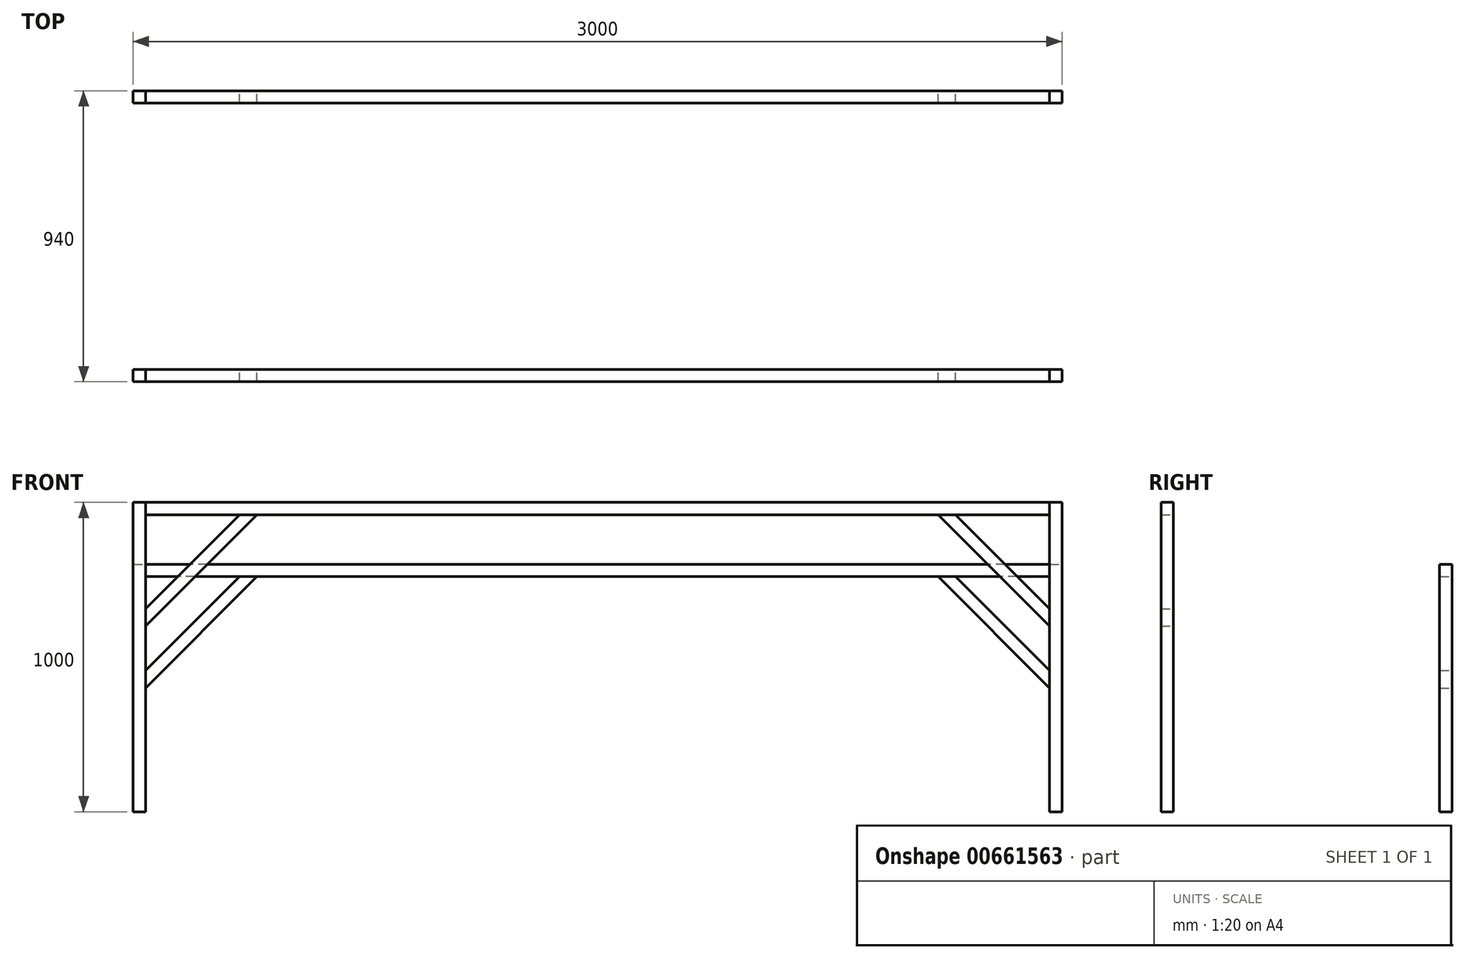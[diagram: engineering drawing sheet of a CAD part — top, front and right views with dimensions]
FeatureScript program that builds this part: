
annotation { "Feature Type Name" : "Feature", "Feature Type Description" : "" }
export const myFeature = defineFeature(function(context is Context, id is Id, definition is map)
    precondition{}
    {
        {
            var Q0;
            Q0=qCreatedBy(makeId("Top.planeOp"),FACE);
            var sketch = newSketch(context, id + "F0", { "sketchPlane" : qUnion([Q0])});
            skLineSegment(sketch, "E0.bottom", {"start": v(0, 0) * mm, "end": v(40, 0) * mm});
            skLineSegment(sketch, "E0.top", {"start": v(0, -40) * mm, "end": v(40, -40) * mm});
            skLineSegment(sketch, "E0.left", {"start": v(0, 0) * mm, "end": v(0, -40) * mm});
            skLineSegment(sketch, "E0.right", {"start": v(40, 0) * mm, "end": v(40, -40) * mm});
            skLineSegment(sketch, "E1.0.1.0", {"start": v(40, -900) * mm, "end": v(40, -940) * mm});
            skLineSegment(sketch, "E1.0.1.1", {"start": v(0, -900) * mm, "end": v(0, -940) * mm});
            skLineSegment(sketch, "E1.0.1.2", {"start": v(0, -900) * mm, "end": v(40, -900) * mm});
            skLineSegment(sketch, "E1.0.1.3", {"start": v(0, -940) * mm, "end": v(40, -940) * mm});
            skLineSegment(sketch, "E1.1.0.0", {"start": v(3000, 0) * mm, "end": v(3000, -40) * mm});
            skLineSegment(sketch, "E1.1.0.1", {"start": v(2960, 0) * mm, "end": v(2960, -40) * mm});
            skLineSegment(sketch, "E1.1.0.2", {"start": v(2960, 0) * mm, "end": v(3000, 0) * mm});
            skLineSegment(sketch, "E1.1.0.3", {"start": v(2960, -40) * mm, "end": v(3000, -40) * mm});
            skLineSegment(sketch, "E1.1.1.0", {"start": v(3000, -900) * mm, "end": v(3000, -940) * mm});
            skLineSegment(sketch, "E1.1.1.1", {"start": v(2960, -900) * mm, "end": v(2960, -940) * mm});
            skLineSegment(sketch, "E1.1.1.2", {"start": v(2960, -900) * mm, "end": v(3000, -900) * mm});
            skLineSegment(sketch, "E1.1.1.3", {"start": v(2960, -940) * mm, "end": v(3000, -940) * mm});
            skLineSegment(sketch, "E1.direction1", {"start": v(0, -40) * mm, "end": v(2960, -40) * mm, "construction": true});
            skLineSegment(sketch, "E1.direction2", {"start": v(0, -40) * mm, "end": v(0, -940) * mm, "construction": true});
            skSolve(sketch);
        }
        {
            var Q0;
            Q0=makeQuery(id+"F0.imprint","IMPRINT",FACE,{"disambiguationData":[TD([[makeQuery(id+"F0.imprint","IMPRINT",EDGE,{"derivedFrom":sQuery(id+"F0.wireOp",EDGE,"E0.bottom")}),-1.0]])]});
            var Q1;
            Q1=makeQuery(id+"F0.imprint","IMPRINT",FACE,{"disambiguationData":[TD([[makeQuery(id+"F0.imprint","IMPRINT",EDGE,{"derivedFrom":sQuery(id+"F0.wireOp",EDGE,"E1.1.0.0")}),-1.0]])]});
            extrude(context, id + "F1", {"entities" : qUnion([Q0, Q1]), "depth" : 800 * mm, "offsetDistance" : 25 * mm});
        }
        {
            var Q0;
            Q0=makeQuery(id+"F0.imprint","IMPRINT",FACE,{"disambiguationData":[TD([[makeQuery(id+"F0.imprint","IMPRINT",EDGE,{"derivedFrom":sQuery(id+"F0.wireOp",EDGE,"E1.0.1.0")}),-1.0]])]});
            var Q1;
            Q1=makeQuery(id+"F0.imprint","IMPRINT",FACE,{"disambiguationData":[TD([[makeQuery(id+"F0.imprint","IMPRINT",EDGE,{"derivedFrom":sQuery(id+"F0.wireOp",EDGE,"E1.1.1.0")}),-1.0]])]});
            extrude(context, id + "F2", {"entities" : qUnion([Q0, Q1]), "depth" : 1000 * mm, "offsetDistance" : 25 * mm});
        }
        {
            var Q0;
            Q0=makeQuery(id+"F1.opExtrude","SWEPT_FACE",FACE,{"disambiguationData":[OSD([sQuery(id+"F0.wireOp",EDGE,"E0.right")])]});
            var sketch = newSketch(context, id + "F3", { "sketchPlane" : qUnion([Q0])});
            skLineSegment(sketch, "E2.bottom", {"start": v(-40, 800) * mm, "end": v(0, 800) * mm});
            skLineSegment(sketch, "E2.top", {"start": v(-40, 760) * mm, "end": v(0, 760) * mm});
            skLineSegment(sketch, "E2.left", {"start": v(-40, 800) * mm, "end": v(-40, 760) * mm});
            skLineSegment(sketch, "E2.right", {"start": v(0, 800) * mm, "end": v(0, 760) * mm});
            skSolve(sketch);
        }
        {
            var Q0;
            Q0=makeQuery(id+"F3.imprint","IMPRINT",FACE,{"disambiguationData":[TD([[makeQuery(id+"F3.imprint","IMPRINT",EDGE,{"derivedFrom":sQuery(id+"F3.wireOp",EDGE,"E2.bottom")}),1.0]])]});
            extrude(context, id + "F4", {"entities" : qUnion([Q0]), "endBound" : BoundingType.UP_TO_NEXT, "depth" : 25 * mm, "offsetDistance" : 25 * mm});
        }
        {
            var Q0;
            Q0=makeQuery(id+"F2.opExtrude","SWEPT_FACE",FACE,{"disambiguationData":[OSD([sQuery(id+"F0.wireOp",EDGE,"E1.0.1.0")])]});
            var sketch = newSketch(context, id + "F5", { "sketchPlane" : qUnion([Q0])});
            skLineSegment(sketch, "E3.bottom", {"start": v(-940, 1000) * mm, "end": v(-900, 1000) * mm});
            skLineSegment(sketch, "E3.top", {"start": v(-940, 960) * mm, "end": v(-900, 960) * mm});
            skLineSegment(sketch, "E3.left", {"start": v(-940, 1000) * mm, "end": v(-940, 960) * mm});
            skLineSegment(sketch, "E3.right", {"start": v(-900, 1000) * mm, "end": v(-900, 960) * mm});
            skSolve(sketch);
        }
        {
            var Q0;
            Q0=makeQuery(id+"F5.imprint","IMPRINT",FACE,{"disambiguationData":[TD([[makeQuery(id+"F5.imprint","IMPRINT",EDGE,{"derivedFrom":sQuery(id+"F5.wireOp",EDGE,"E3.bottom")}),1.0]])]});
            extrude(context, id + "F6", {"entities" : qUnion([Q0]), "endBound" : BoundingType.UP_TO_NEXT, "depth" : 25 * mm, "offsetDistance" : 25 * mm});
        }
        {
            var Q0;
            Q0=makeQuery(id+"F1.opExtrude","SWEPT_FACE",FACE,{"disambiguationData":[OSD([sQuery(id+"F0.wireOp",EDGE,"E0.bottom")])]});
            var sketch = newSketch(context, id + "F7", { "sketchPlane" : qUnion([Q0])});
            skLineSegment(sketch, "E4", {"start": v(-40, 456.57) * mm, "end": v(-343.43, 760) * mm});
            skLineSegment(sketch, "E5", {"start": v(-343.43, 760) * mm, "end": v(-400, 760) * mm});
            skLineSegment(sketch, "E6", {"start": v(-400, 760) * mm, "end": v(-40, 400) * mm});
            skLineSegment(sketch, "E7", {"start": v(-40, 400) * mm, "end": v(-40, 456.57) * mm});
            skSolve(sketch);
        }
        {
            var Q0;
            Q0=makeQuery(id+"F7.imprint","IMPRINT",FACE,{"disambiguationData":[TD([[makeQuery(id+"F7.imprint","IMPRINT",EDGE,{"derivedFrom":sQuery(id+"F7.wireOp",EDGE,"E4")}),1.0]])]});
            extrude(context, id + "F8", {"entities" : qUnion([Q0]), "oppositeDirection" : true, "depth" : 40 * mm, "offsetDistance" : 25 * mm});
        }
        {
            var Q0;
            Q0=qCreatedBy(makeId("Right.planeOp"),FACE);
            cPlane(context, id + "F9", {"entities" : qUnion([Q0]), "cplaneType" : CPlaneType.OFFSET, "offset" : 3000 / 2 * mm, "width" : 150 * mm, "height" : 150 * mm});
        }
        {
            var Q0;
            Q0=makeQuery(id+"F8.opExtrude","SWEPT_BODY",BODY,{"disambiguationData":[OSD([sQuery(id+"F7.wireOp",EDGE,"E4"),sQuery(id+"F7.wireOp",EDGE,"E5"),sQuery(id+"F7.wireOp",EDGE,"E6"),sQuery(id+"F7.wireOp",EDGE,"E7")])]});
            var Q1;
            Q1=sQuery(id+"F0.wireOp",EDGE,"E1.direction2");
            transform(context, id + "F10", {"entities" : qUnion([Q0]), "transformType" : TransformType.TRANSLATION_3D, "dx" : 0 * mm, "dy" : -900 * mm, "dz" : 200 * mm, "makeCopy" : true});
        }
        {
            var Q0;
            Q0=makeQuery(id+"F10.opPattern","COPY",BODY,{"derivedFrom":makeQuery(id+"F8.opExtrude","SWEPT_BODY",BODY,{"disambiguationData":[OSD([sQuery(id+"F7.wireOp",EDGE,"E4"),sQuery(id+"F7.wireOp",EDGE,"E5"),sQuery(id+"F7.wireOp",EDGE,"E6"),sQuery(id+"F7.wireOp",EDGE,"E7")])]}),"instanceName":"1"});
            var Q1;
            Q1=makeQuery(id+"F8.opExtrude","SWEPT_BODY",BODY,{"disambiguationData":[OSD([sQuery(id+"F7.wireOp",EDGE,"E4"),sQuery(id+"F7.wireOp",EDGE,"E5"),sQuery(id+"F7.wireOp",EDGE,"E6"),sQuery(id+"F7.wireOp",EDGE,"E7")])]});
            var Q2;
            Q2=qCreatedBy(id+"F9.planeOp",FACE);
            mirror(context, id + "F11", {"entities" : qUnion([Q0, Q1]), "mirrorPlane" : qUnion([Q2])});
        }
    });
